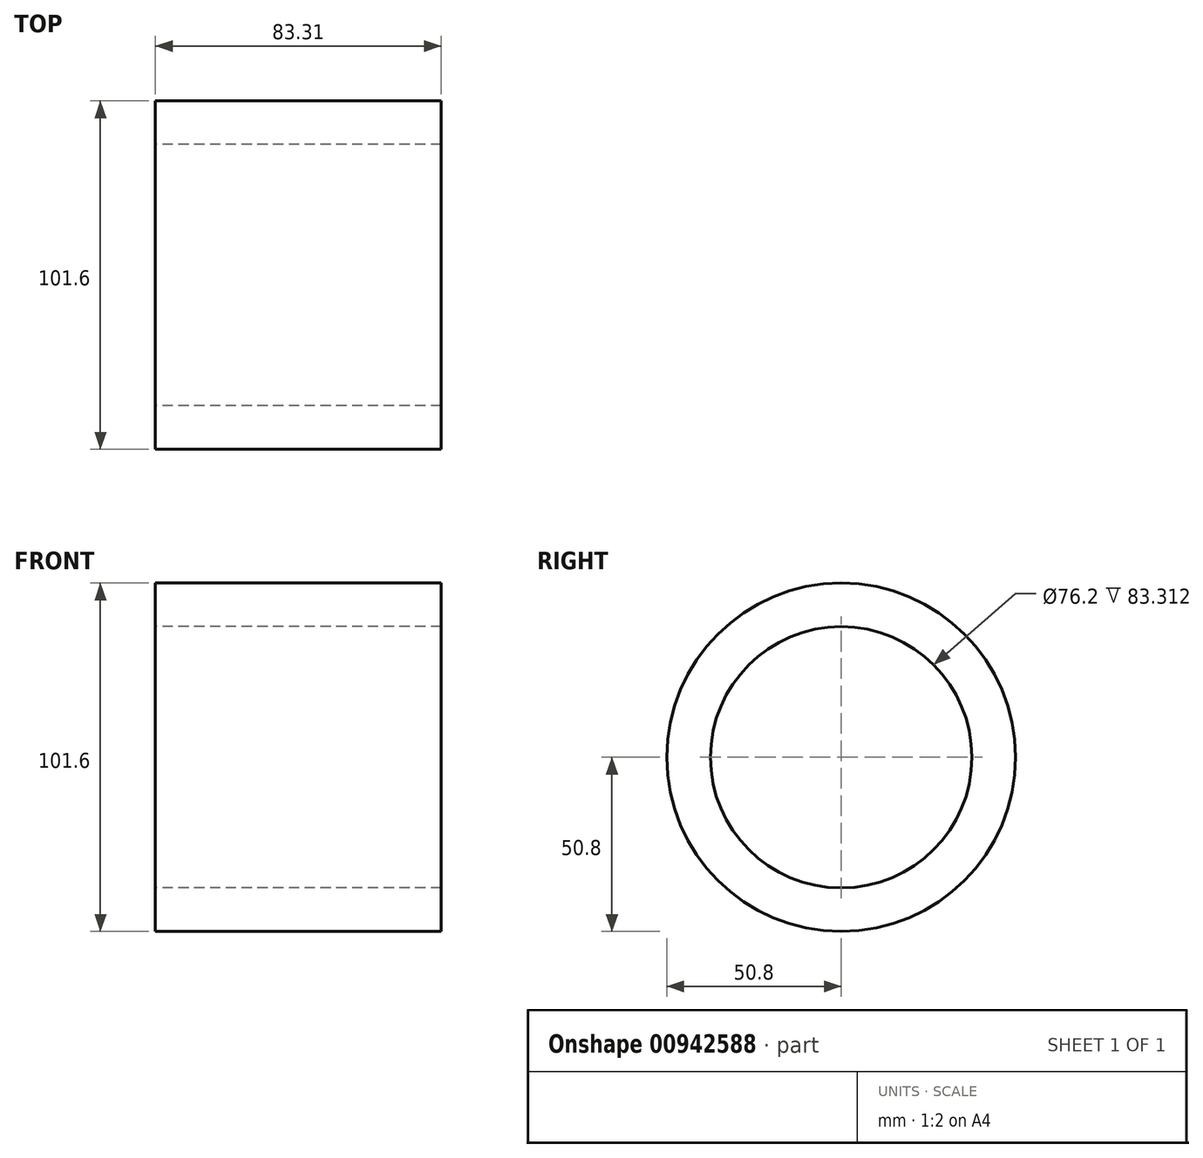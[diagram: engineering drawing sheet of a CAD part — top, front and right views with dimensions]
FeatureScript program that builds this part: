
annotation { "Feature Type Name" : "Feature", "Feature Type Description" : "" }
export const myFeature = defineFeature(function(context is Context, id is Id, definition is map)
    precondition{}
    {
        {
            var Q0;
            Q0=qCreatedBy(makeId("Right.planeOp"),FACE);
            var sketch = newSketch(context, id + "F0", { "sketchPlane" : qUnion([Q0])});
            skCircle(sketch, "E0", {"center": v(0, 0) * mm, "radius": 50.8 * mm});
            skCircle(sketch, "E1", {"center": v(0, 0) * mm, "radius": 38.1 * mm});
            skSolve(sketch);
        }
        {
            var Q0;
            Q0 = qSketchRegion(id + "F0", true);
            extrude(context, id + "F1", {"entities" : qUnion([Q0]), "depth" : 83.31 * mm, "offsetDistance" : 25.4 * mm});
        }
    });
